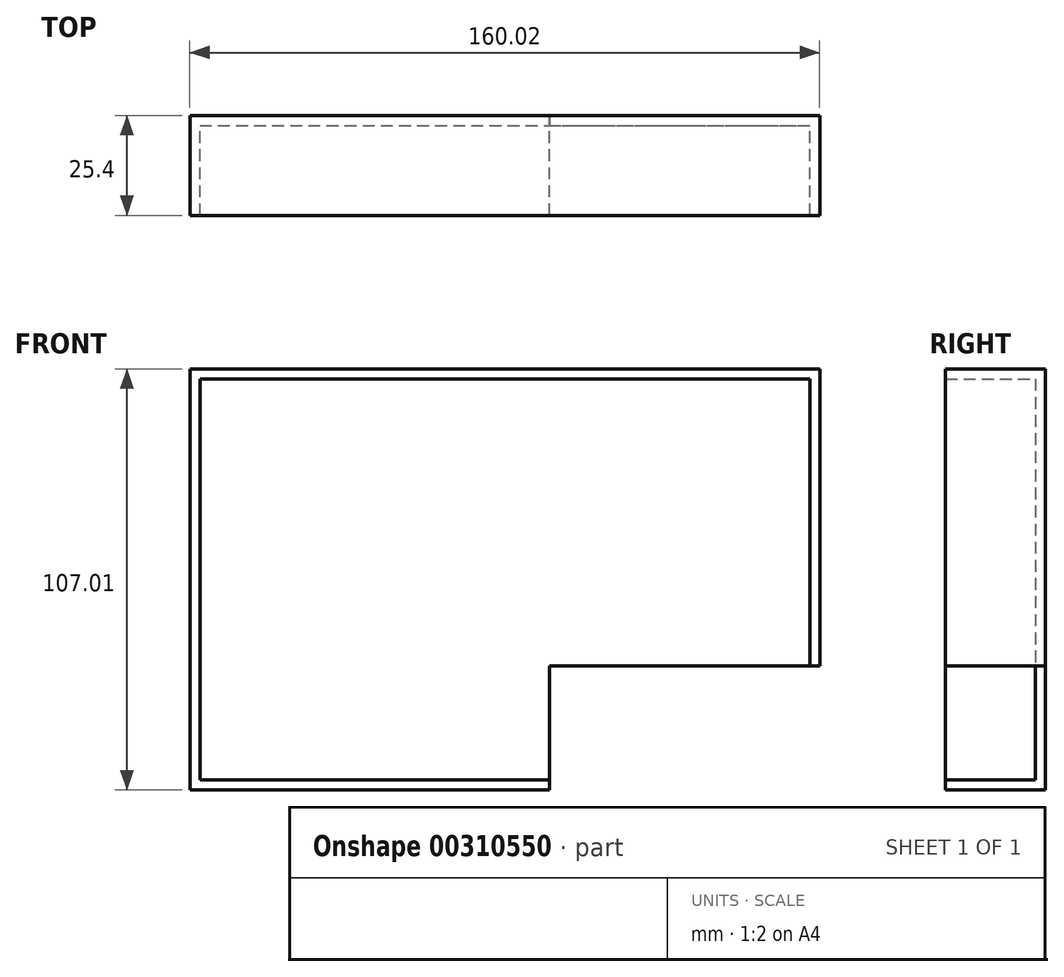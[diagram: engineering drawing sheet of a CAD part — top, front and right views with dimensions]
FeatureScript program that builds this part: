
annotation { "Feature Type Name" : "Feature", "Feature Type Description" : "" }
export const myFeature = defineFeature(function(context is Context, id is Id, definition is map)
    precondition{}
    {
        {
            var Q0;
            Q0=qCreatedBy(makeId("Front.planeOp"),FACE);
            var sketch = newSketch(context, id + "F0", { "sketchPlane" : qUnion([Q0])});
            skLineSegment(sketch, "E0", {"start": v(-91.36, 47.59) * mm, "end": v(-91.36, -59.42) * mm});
            skLineSegment(sketch, "E1", {"start": v(-91.36, 80.58) * mm, "end": v(-7.2, 80.58) * mm});
            skLineSegment(sketch, "E2", {"start": v(-7.2, 107.48) * mm, "end": v(61.37, 107.48) * mm});
            skLineSegment(sketch, "E3", {"start": v(0, 47.59) * mm, "end": v(0, -59.42) * mm});
            skLineSegment(sketch, "E4", {"start": v(-91.36, -59.42) * mm, "end": v(68.66, -59.42) * mm});
            skLineSegment(sketch, "E5", {"start": v(-91.36, 47.59) * mm, "end": v(68.66, 47.59) * mm});
            skLineSegment(sketch, "E6", {"start": v(68.66, 47.59) * mm, "end": v(68.66, -59.42) * mm});
            skSolve(sketch);
        }
        {
            var Q0;
            {var subQ0=sQuery(id+"F0.wireOp",EDGE,"E0");Q0=makeQuery(id+"F0.imprint","IMPRINT",FACE,{"disambiguationData":[TD([[makeQuery(id+"F0.imprint","IMPRINT",EDGE,{"derivedFrom":subQ0}),1.0]])]});}
            var Q1;
            {var subQ0=sQuery(id+"F0.wireOp",EDGE,"E3");Q1=makeQuery(id+"F0.imprint","IMPRINT",FACE,{"disambiguationData":[TD([[makeQuery(id+"F0.imprint","IMPRINT",EDGE,{"derivedFrom":subQ0}),1.0]])]});}
            extrude(context, id + "F1", {"entities" : qUnion([Q0, Q1]), "depth" : 25.4 * mm});
        }
        {
            var Q0;
            Q0=makeQuery(id+"F1.opExtrude","CAP_FACE",FACE,{"disambiguationData":[OSD([sQuery(id+"F0.wireOp",EDGE,"E0"),sQuery(id+"F0.wireOp",EDGE,"E4"),sQuery(id+"F0.wireOp",EDGE,"E5"),sQuery(id+"F0.wireOp",EDGE,"E6")])],"isStart":false});
            shell(context, id + "F2", {"entities" : qUnion([Q0]), "thickness" : 2.54 * mm});
        }
        {
            var Q0;
            Q0=makeQuery(id+"F1.opExtrude","SWEPT_FACE",FACE,{"disambiguationData":[OSD([sQuery(id+"F0.wireOp",EDGE,"E4")])]});
            var sketch = newSketch(context, id + "F3", { "sketchPlane" : qUnion([Q0])});
            skLineSegment(sketch, "E7", {"start": v(0, 0) * mm, "end": v(0, 25.4) * mm});
            skLineSegment(sketch, "E8", {"start": v(0, 25.4) * mm, "end": v(68.66, 25.4) * mm});
            skLineSegment(sketch, "E9", {"start": v(68.66, 25.4) * mm, "end": v(68.66, 0) * mm});
            skLineSegment(sketch, "E10", {"start": v(68.66, 0) * mm, "end": v(0, 0) * mm});
            skSolve(sketch);
        }
        {
            var Q0;
            Q0=makeQuery(id+"F3.imprint","IMPRINT",FACE,{"disambiguationData":[TD([[makeQuery(id+"F3.imprint","IMPRINT",EDGE,{"derivedFrom":sQuery(id+"F3.wireOp",EDGE,"E7")}),-1.0]])]});
            extrude(context, id + "F4", {"entities" : qUnion([Q0]), "operationType" : NewBodyOperationType.REMOVE, "endBound" : BoundingType.SYMMETRIC, "oppositeDirection" : true, "depth" : 63 * mm});
        }
    });
